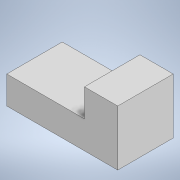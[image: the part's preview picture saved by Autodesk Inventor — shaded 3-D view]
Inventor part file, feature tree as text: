
AUTODESK INVENTOR PART (.ipt)
format: ipt  version: 2022 (Build 260153000, 153)  size: 92,160 bytes
history: native  units: mm
features: other x1, extrude x1, sketch x1
ambient origin geometry x8: Origin, YZ Plane, XZ Plane, XY Plane, X Axis, Y Axis, Z Axis, Center Point
bodies: Body1 (feature_tree)
feature tree (3):
  other  "Sólido1"
  extrude  "Extrusão1"  Depth=30.0mm
  sketch  "Esboço1"  dims[d0=60.0mm d2=30.0mm d3=18.0mm d4=15.0mm d5=30.0mm d6=0.0mm]
